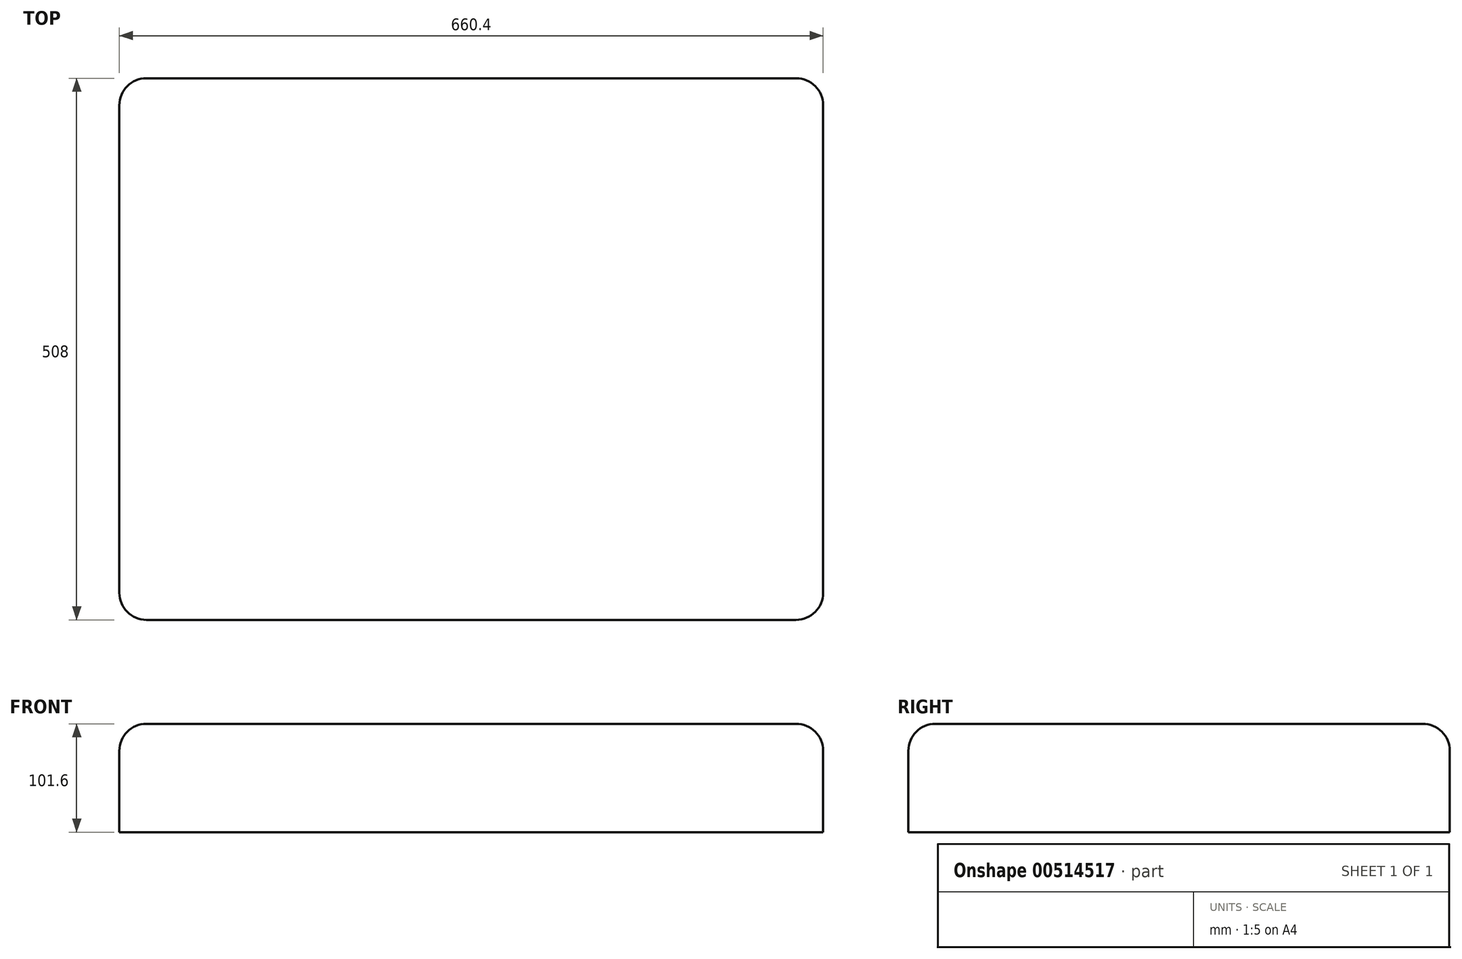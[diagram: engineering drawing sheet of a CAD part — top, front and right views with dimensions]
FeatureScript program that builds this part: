
annotation { "Feature Type Name" : "Feature", "Feature Type Description" : "" }
export const myFeature = defineFeature(function(context is Context, id is Id, definition is map)
    precondition{}
    {
        {
            var Q0;
            Q0=qCreatedBy(makeId("Top.planeOp"),FACE);
            var sketch = newSketch(context, id + "F0", { "sketchPlane" : qUnion([Q0])});
            skLineSegment(sketch, "E0.bottom", {"start": v(330.2, 254) * mm, "end": v(-330.2, 254) * mm});
            skLineSegment(sketch, "E0.top", {"start": v(330.2, -254) * mm, "end": v(-330.2, -254) * mm});
            skLineSegment(sketch, "E0.left", {"start": v(330.2, 254) * mm, "end": v(330.2, -254) * mm});
            skLineSegment(sketch, "E0.right", {"start": v(-330.2, 254) * mm, "end": v(-330.2, -254) * mm});
            skPoint(sketch, "E0.middle", {"position": v(0, 0) * mm});
            skSolve(sketch);
        }
        {
            var Q0;
            Q0=makeQuery(id+"F0.imprint","IMPRINT",FACE,{"disambiguationData":[TD([[makeQuery(id+"F0.imprint","IMPRINT",EDGE,{"derivedFrom":sQuery(id+"F0.wireOp",EDGE,"E0.bottom")}),1.0]])]});
            extrude(context, id + "F1", {"entities" : qUnion([Q0]), "depth" : 101.6 * mm, "offsetDistance" : 25.4 * mm});
        }
        {
            var Q0;
            Q0=makeQuery(id+"F1.opExtrude","CAP_FACE",FACE,{"disambiguationData":[OSD([sQuery(id+"F0.wireOp",EDGE,"E0.bottom"),sQuery(id+"F0.wireOp",EDGE,"E0.top"),sQuery(id+"F0.wireOp",EDGE,"E0.left"),sQuery(id+"F0.wireOp",EDGE,"E0.right")])],"isStart":false});
            var Q1;
            Q1=makeQuery(id+"F1.opExtrude","SWEPT_EDGE",EDGE,{"disambiguationData":[OSD([sQuery(id+"F0.wireOp",EDGE,"E0.bottom"),sQuery(id+"F0.wireOp",EDGE,"E0.right")])]});
            var Q2;
            Q2=makeQuery(id+"F1.opExtrude","SWEPT_EDGE",EDGE,{"disambiguationData":[OSD([sQuery(id+"F0.wireOp",EDGE,"E0.bottom"),sQuery(id+"F0.wireOp",EDGE,"E0.left")])]});
            var Q3;
            Q3=makeQuery(id+"F1.opExtrude","SWEPT_EDGE",EDGE,{"disambiguationData":[OSD([sQuery(id+"F0.wireOp",EDGE,"E0.top"),sQuery(id+"F0.wireOp",EDGE,"E0.left")])]});
            var Q4;
            Q4=makeQuery(id+"F1.opExtrude","SWEPT_EDGE",EDGE,{"disambiguationData":[OSD([sQuery(id+"F0.wireOp",EDGE,"E0.top"),sQuery(id+"F0.wireOp",EDGE,"E0.right")])]});
            fillet(context, id + "F2", {"entities" : qUnion([Q0, Q1, Q2, Q3, Q4]), "radius" : 25.4 * mm, "tangentPropagation" : true, "allowEdgeOverflow" : false});
        }
    });
